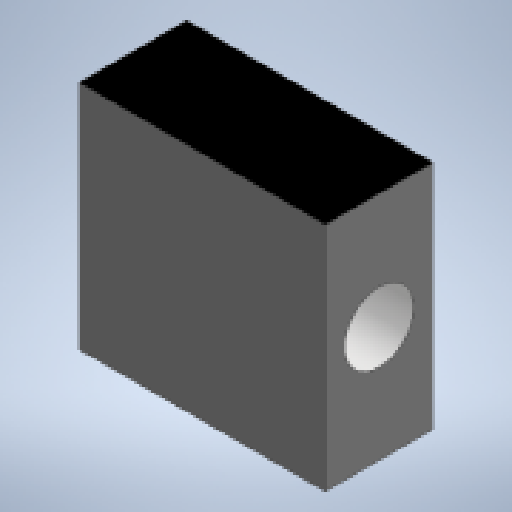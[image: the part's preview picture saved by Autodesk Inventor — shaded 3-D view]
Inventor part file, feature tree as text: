
AUTODESK INVENTOR PART (.ipt)
format: ipt  version: 2023 (Build 270158000, 158)  size: 133,120 bytes
history: native  units: in
note: dims shown in document units (in); Inventor stores cm internally (conversion verified against a paired STEP export)
features: extrude x2, sketch x2
ambient origin geometry x8: Origin, YZ Plane, XZ Plane, XY Plane, X Axis, Y Axis, Z Axis, Center Point
bodies: Solid1 (feature_tree)
feature tree (4):
  extrude  "Extrusion1"  Depth=1.1811in
  extrude  "Extrusion2"  Depth=0.5512in
  sketch  "Sketch1"  dims[d0=1.2598in d1=1.1811in]
  sketch  "Sketch2"  dims[d2=0.5512in d3=0.0in d4=0.3543in d5=0.0in d6=0.0in]
